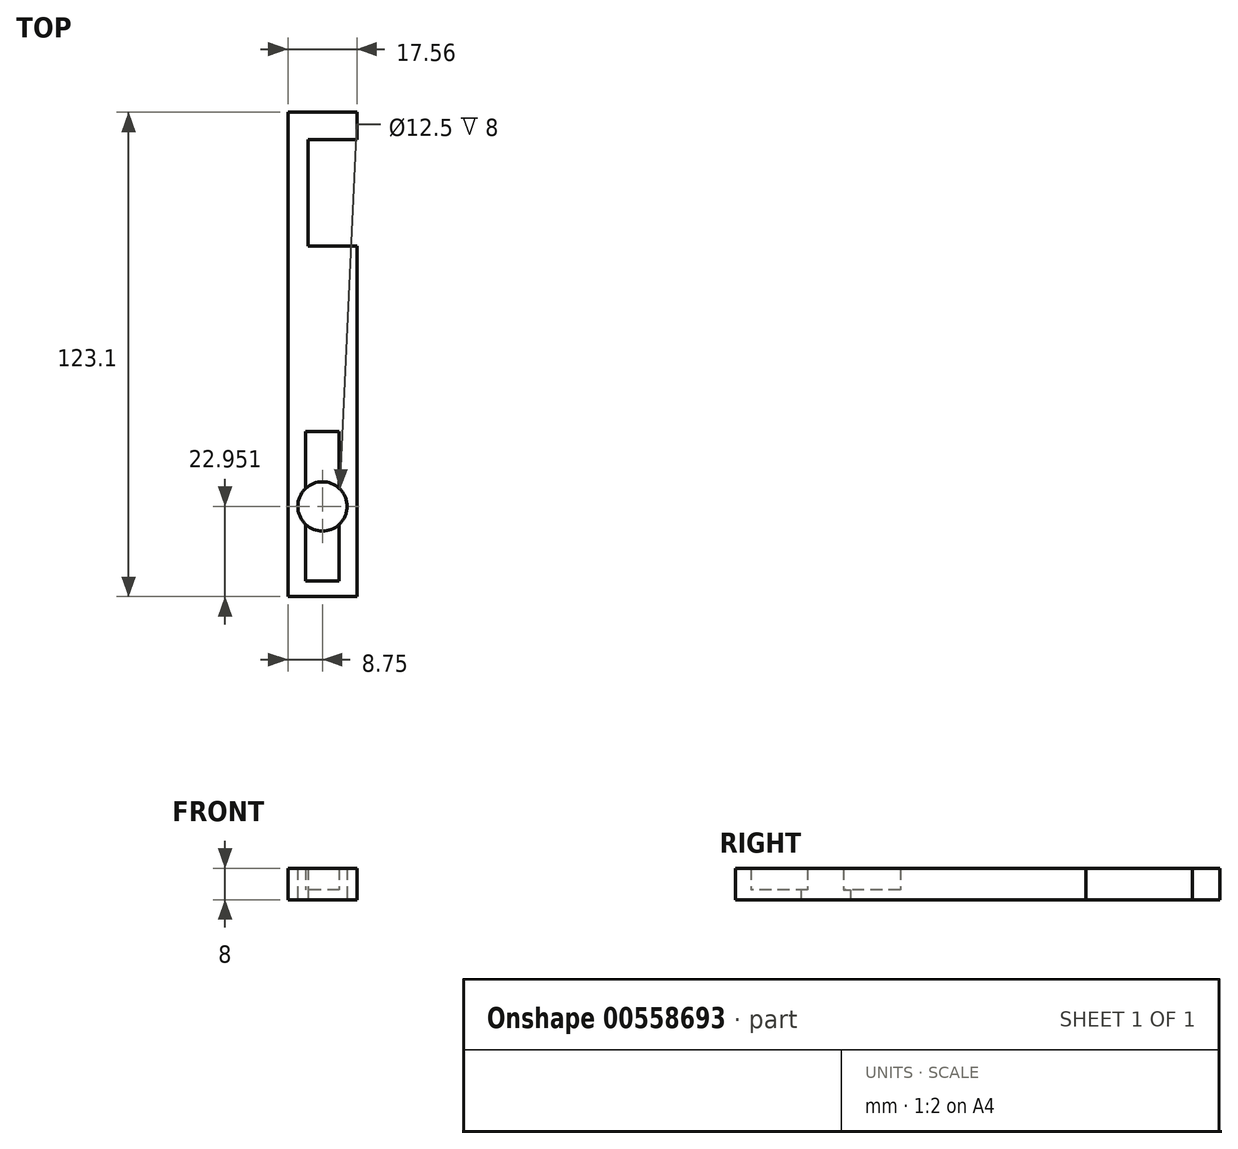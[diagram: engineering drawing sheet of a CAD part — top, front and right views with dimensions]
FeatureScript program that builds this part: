
annotation { "Feature Type Name" : "Feature", "Feature Type Description" : "" }
export const myFeature = defineFeature(function(context is Context, id is Id, definition is map)
    precondition{}
    {
        {
            var Q0;
            Q0=qCreatedBy(makeId("Top.planeOp"),FACE);
            var sketch = newSketch(context, id + "F0", { "sketchPlane" : qUnion([Q0])});
            skLineSegment(sketch, "E0.bottom", {"start": v(8.75, 44.55) * mm, "end": v(-8.75, 44.55) * mm});
            skLineSegment(sketch, "E0.top", {"start": v(8.75, -44.55) * mm, "end": v(-8.75, -44.55) * mm});
            skLineSegment(sketch, "E0.left", {"start": v(8.75, 44.55) * mm, "end": v(8.75, -44.55) * mm});
            skLineSegment(sketch, "E0.right", {"start": v(-8.75, 44.55) * mm, "end": v(-8.75, -44.55) * mm});
            skPoint(sketch, "E0.middle", {"position": v(0, 0) * mm});
            skLineSegment(sketch, "E1.bottom", {"start": v(4.25, -2.6) * mm, "end": v(-4.25, -2.6) * mm});
            skLineSegment(sketch, "E1.top", {"start": v(4.25, -40.6) * mm, "end": v(-4.25, -40.6) * mm});
            skLineSegment(sketch, "E1.left", {"start": v(4.25, -2.6) * mm, "end": v(4.25, -40.6) * mm});
            skLineSegment(sketch, "E1.right", {"start": v(-4.25, -2.6) * mm, "end": v(-4.25, -40.6) * mm});
            skPoint(sketch, "E1.middle", {"position": v(0, -21.6) * mm});
            skCircle(sketch, "E2", {"center": v(0, -21.6) * mm, "radius": 6.25 * mm});
            skLineSegment(sketch, "E3.bottom", {"start": v(-8.75, 44.55) * mm, "end": v(-3.75, 44.55) * mm});
            skLineSegment(sketch, "E4.bottom", {"start": v(8.75, 44.55) * mm, "end": v(3.75, 44.55) * mm});
            skLineSegment(sketch, "E5.bottom", {"start": v(-8.75, 44.55) * mm, "end": v(-3.7, 44.55) * mm});
            skLineSegment(sketch, "E5.top", {"start": v(-8.75, 78.55) * mm, "end": v(-3.7, 78.55) * mm});
            skLineSegment(sketch, "E5.left", {"start": v(-8.75, 44.55) * mm, "end": v(-8.75, 78.55) * mm});
            skLineSegment(sketch, "E5.right", {"start": v(-3.7, 44.55) * mm, "end": v(-3.7, 78.55) * mm});
            skLineSegment(sketch, "E6.bottom", {"start": v(-3.7, 78.55) * mm, "end": v(8.8, 78.55) * mm});
            skLineSegment(sketch, "E6.top", {"start": v(-3.7, 71.55) * mm, "end": v(8.8, 71.55) * mm});
            skLineSegment(sketch, "E6.left", {"start": v(-3.7, 78.55) * mm, "end": v(-3.7, 71.55) * mm});
            skLineSegment(sketch, "E6.right", {"start": v(8.8, 78.55) * mm, "end": v(8.8, 71.55) * mm});
            skSolve(sketch);
        }
        {
            var Q0;
            Q0=makeQuery(id+"F0.imprint","IMPRINT",FACE,{"disambiguationData":[TD([[makeQuery(id+"F0.imprint","IMPRINT",EDGE,{"derivedFrom":sQuery(id+"F0.wireOp",EDGE,"Pqc5xqcg-Qgv8-XXyU-ekZD-nZ5gzvdi3LpR.bottom")}),-1.0]])]});
            var Q1;
            Q1=makeQuery(id+"F0.imprint","IMPRINT",FACE,{"disambiguationData":[TD([[makeQuery(id+"F0.imprint","IMPRINT",EDGE,{"derivedFrom":sQuery(id+"F0.wireOp",EDGE,"E3.bottom")}),1.0]])]});
            var Q2;
            Q2=makeQuery(id+"F0.imprint","IMPRINT",FACE,{"disambiguationData":[TD([[makeQuery(id+"F0.imprint","IMPRINT",EDGE,{"derivedFrom":sQuery(id+"F0.wireOp",EDGE,"E0.bottom")}),1.0]])]});
            var Q3;
            Q3=makeQuery(id+"F0.imprint","IMPRINT",FACE,{"disambiguationData":[TD([[makeQuery(id+"F0.imprint","IMPRINT",EDGE,{"derivedFrom":sQuery(id+"F0.wireOp",EDGE,"E4.bottom")}),-1.0]])]});
            var Q4;
            Q4=makeQuery(id+"F0.imprint","IMPRINT",FACE,{"disambiguationData":[TD([[makeQuery(id+"F0.imprint","IMPRINT",EDGE,{"derivedFrom":sQuery(id+"F0.wireOp",EDGE,"HnQft3v9-mSai-PtbU-x4zt-C10cOCln6Zu0.bottom")}),1.0]])]});
            var Q5;
            Q5=makeQuery(id+"F0.imprint","IMPRINT",FACE,{"disambiguationData":[TD([[makeQuery(id+"F0.imprint","IMPRINT",EDGE,{"derivedFrom":sQuery(id+"F0.wireOp",EDGE,"E5.top")}),-1.0]])]});
            var Q6;
            Q6=makeQuery(id+"F0.imprint","IMPRINT",FACE,{"disambiguationData":[TD([[makeQuery(id+"F0.imprint","IMPRINT",EDGE,{"derivedFrom":sQuery(id+"F0.wireOp",EDGE,"E6.bottom")}),-1.0]])]});
            extrude(context, id + "F1", {"entities" : qUnion([Q0, Q1, Q2, Q3, Q4, Q5, Q6]), "depth" : 8 * mm, "offsetDistance" : 25 * mm});
        }
        {
            var Q0;
            {var subQ0=sQuery(id+"F0.wireOp",EDGE,"E1.top");Q0=makeQuery(id+"F0.imprint","IMPRINT",FACE,{"disambiguationData":[TD([[makeQuery(id+"F0.imprint","IMPRINT",EDGE,{"derivedFrom":subQ0}),-1.0]])]});}
            var Q1;
            {var subQ0=sQuery(id+"F0.wireOp",EDGE,"E2");var subQ1=sQuery(id+"F0.wireOp",EDGE,"E1.left");var subQ2=makeQuery(id+"F0.imprint","INTERSECT",VERTEX,{"disambiguationData":[OD(0.0)],"derivedFrom":[subQ1,subQ0]});Q1=makeQuery(id+"F0.imprint","IMPRINT",FACE,{"disambiguationData":[TD([[makeQuery(id+"F0.imprint","IMPRINT",EDGE,{"disambiguationData":[TD([[subQ2,-1.0]])],"derivedFrom":subQ1}),-1.0]])]});}
            var Q2;
            {var subQ0=sQuery(id+"F0.wireOp",EDGE,"E1.bottom");Q2=makeQuery(id+"F0.imprint","IMPRINT",FACE,{"disambiguationData":[TD([[makeQuery(id+"F0.imprint","IMPRINT",EDGE,{"derivedFrom":subQ0}),1.0]])]});}
            var Q3;
            {var subQ0=sQuery(id+"F0.wireOp",EDGE,"E2");var subQ1=sQuery(id+"F0.wireOp",EDGE,"E1.left");var subQ2=makeQuery(id+"F0.imprint","INTERSECT",VERTEX,{"disambiguationData":[OD(0.0)],"derivedFrom":[subQ1,subQ0]});Q3=makeQuery(id+"F0.imprint","IMPRINT",FACE,{"disambiguationData":[TD([[makeQuery(id+"F0.imprint","IMPRINT",EDGE,{"disambiguationData":[TD([[subQ2,-1.0]])],"derivedFrom":subQ1}),1.0]])]});}
            var Q4;
            {var subQ0=sQuery(id+"F0.wireOp",EDGE,"E2");var subQ1=sQuery(id+"F0.wireOp",EDGE,"E1.right");var subQ2=makeQuery(id+"F0.imprint","INTERSECT",VERTEX,{"disambiguationData":[OD(0.0)],"derivedFrom":[subQ1,subQ0]});Q4=makeQuery(id+"F0.imprint","IMPRINT",FACE,{"disambiguationData":[TD([[makeQuery(id+"F0.imprint","IMPRINT",EDGE,{"disambiguationData":[TD([[subQ2,-1.0]])],"derivedFrom":subQ1}),-1.0]])]});}
            extrude(context, id + "F2", {"entities" : qUnion([Q0, Q1, Q2, Q3, Q4]), "operationType" : NewBodyOperationType.ADD, "depth" : 2.5 * mm, "offsetDistance" : 25 * mm});
        }
    });
